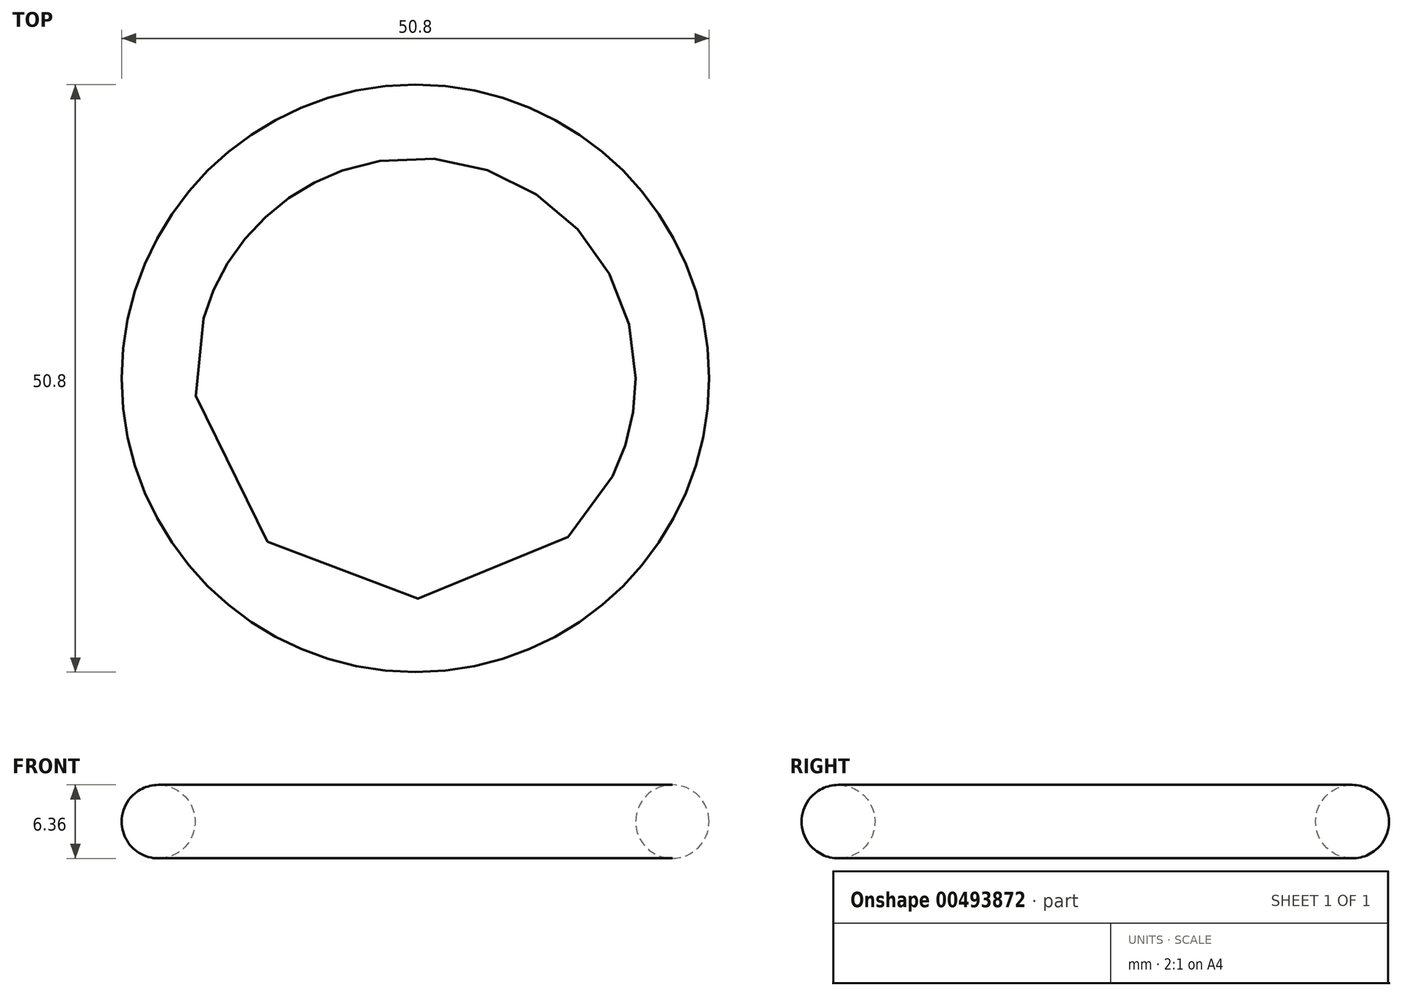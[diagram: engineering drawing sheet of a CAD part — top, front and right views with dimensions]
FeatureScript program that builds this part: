
annotation { "Feature Type Name" : "Feature", "Feature Type Description" : "" }
export const myFeature = defineFeature(function(context is Context, id is Id, definition is map)
    precondition{}
    {
        {
            var Q0;
            Q0=qCreatedBy(makeId("Front.planeOp"),FACE);
            var sketch = newSketch(context, id + "F0", { "sketchPlane" : qUnion([Q0])});
            skCircle(sketch, "E0", {"center": v(-22.22, 0) * mm, "radius": 3.18 * mm});
            skLineSegment(sketch, "E1", {"start": v(0, 13.05) * mm, "end": v(0, -11.46) * mm, "construction": true});
            skSolve(sketch);
        }
        {
            var Q0;
            Q0 = qSketchRegion(id + "F0", true);
            var Q1;
            Q1=sQuery(id+"F0.wireOp",EDGE,"E1");
            revolve(context, id + "F1", {"entities" : qUnion([Q0]), "axis" : qUnion([Q1]), "revolveType" : RevolveType.FULL});
        }
    });
